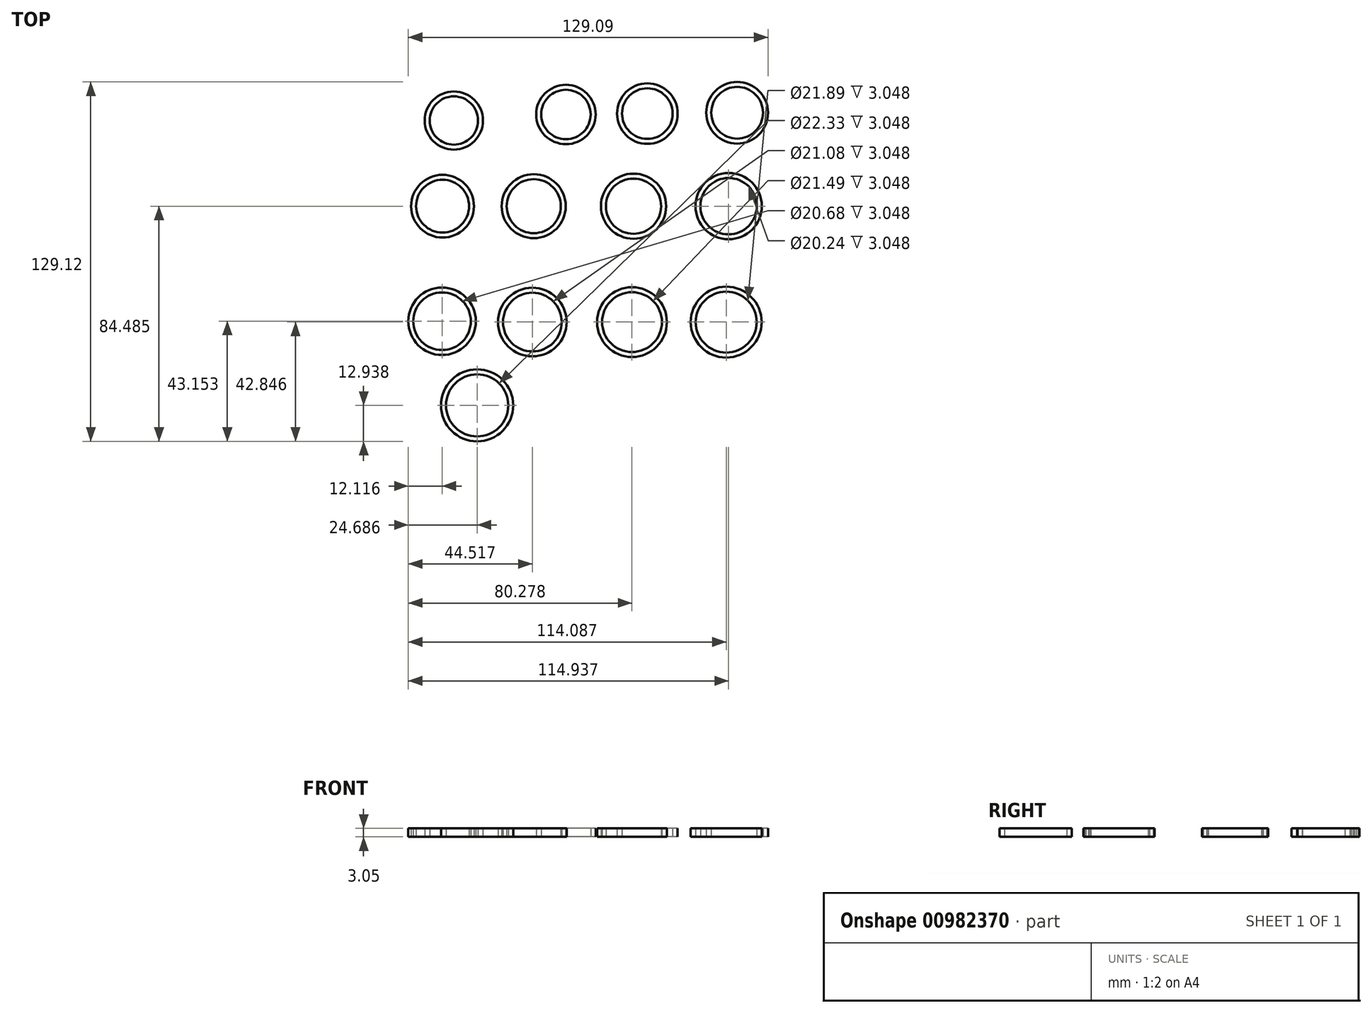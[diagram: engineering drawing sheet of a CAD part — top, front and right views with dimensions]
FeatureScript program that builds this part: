
annotation { "Feature Type Name" : "Feature", "Feature Type Description" : "" }
export const myFeature = defineFeature(function(context is Context, id is Id, definition is map)
    precondition{}
    {
        {
            var Q0;
            Q0=qCreatedBy(makeId("Top.planeOp"),FACE);
            var sketch = newSketch(context, id + "F0", { "sketchPlane" : qUnion([Q0])});
            skCircle(sketch, "E0", {"center": v(-50.04, 48.2) * mm, "radius": 8.67 * mm});
            skCircle(sketch, "E1", {"center": v(-50.04, 48.2) * mm, "radius": 10.45 * mm});
            skSolve(sketch);
        }
        {
            var Q0;
            Q0 = qSketchRegion(id + "F0", true);
            extrude(context, id + "F1", {"entities" : qUnion([Q0]), "depth" : 3.05 * mm, "offsetDistance" : 25.4 * mm});
        }
        {
            var Q0;
            Q0=qCreatedBy(makeId("Top.planeOp"),FACE);
            var sketch = newSketch(context, id + "F2", { "sketchPlane" : qUnion([Q0])});
            skCircle(sketch, "E2", {"center": v(-9.83, 50.36) * mm, "radius": 8.88 * mm});
            skCircle(sketch, "E3", {"center": v(-9.83, 50.36) * mm, "radius": 10.66 * mm});
            skSolve(sketch);
        }
        {
            var Q0;
            Q0 = qSketchRegion(id + "F2", true);
            extrude(context, id + "F3", {"entities" : qUnion([Q0]), "depth" : 3.05 * mm, "offsetDistance" : 25.4 * mm});
        }
        {
            var Q0;
            Q0=qCreatedBy(makeId("Top.planeOp"),FACE);
            var sketch = newSketch(context, id + "F4", { "sketchPlane" : qUnion([Q0])});
            skCircle(sketch, "E4", {"center": v(19.4, 50.69) * mm, "radius": 10.87 * mm});
            skCircle(sketch, "E5", {"center": v(19.4, 50.69) * mm, "radius": 9.1 * mm});
            skSolve(sketch);
        }
        {
            var Q0;
            Q0 = qSketchRegion(id + "F4", true);
            extrude(context, id + "F5", {"entities" : qUnion([Q0]), "depth" : 3.05 * mm, "offsetDistance" : 25.4 * mm});
        }
        {
            var Q0;
            Q0=qCreatedBy(makeId("Top.planeOp"),FACE);
            var sketch = newSketch(context, id + "F6", { "sketchPlane" : qUnion([Q0])});
            skCircle(sketch, "E6", {"center": v(-54.08, 17.43) * mm, "radius": 11.28 * mm});
            skCircle(sketch, "E7", {"center": v(-21.36, 17.43) * mm, "radius": 11.48 * mm});
            skCircle(sketch, "E8", {"center": v(14.44, 17.43) * mm, "radius": 11.7 * mm});
            skCircle(sketch, "E9", {"center": v(48.56, 17.43) * mm, "radius": 11.9 * mm});
            skCircle(sketch, "E10", {"center": v(51.63, 51) * mm, "radius": 11.07 * mm});
            skCircle(sketch, "E11", {"center": v(51.63, 51) * mm, "radius": 9.3 * mm});
            skCircle(sketch, "E12", {"center": v(-54.08, 17.43) * mm, "radius": 9.5 * mm});
            skCircle(sketch, "E13", {"center": v(-21.36, 17.43) * mm, "radius": 9.7 * mm});
            skCircle(sketch, "E14", {"center": v(14.44, 17.43) * mm, "radius": 9.92 * mm});
            skCircle(sketch, "E15", {"center": v(48.56, 17.43) * mm, "radius": 10.12 * mm});
            skSolve(sketch);
        }
        {
            var Q0;
            Q0=makeQuery(id+"F6.imprint","IMPRINT",FACE,{"disambiguationData":[TD([[makeQuery(id+"F6.imprint","IMPRINT",EDGE,{"derivedFrom":sQuery(id+"F6.wireOp",EDGE,"E10")}),1.0]])]});
            extrude(context, id + "F7", {"entities" : qUnion([Q0]), "depth" : 3.05 * mm, "offsetDistance" : 25.4 * mm});
        }
        {
            var Q0;
            Q0=makeQuery(id+"F6.imprint","IMPRINT",FACE,{"disambiguationData":[TD([[makeQuery(id+"F6.imprint","IMPRINT",EDGE,{"derivedFrom":sQuery(id+"F6.wireOp",EDGE,"E6")}),1.0]])]});
            extrude(context, id + "F8", {"entities" : qUnion([Q0]), "depth" : 3.05 * mm, "offsetDistance" : 25.4 * mm});
        }
        {
            var Q0;
            Q0=makeQuery(id+"F6.imprint","IMPRINT",FACE,{"disambiguationData":[TD([[makeQuery(id+"F6.imprint","IMPRINT",EDGE,{"derivedFrom":sQuery(id+"F6.wireOp",EDGE,"E7")}),1.0]])]});
            extrude(context, id + "F9", {"entities" : qUnion([Q0]), "depth" : 3.05 * mm, "offsetDistance" : 25.4 * mm});
        }
        {
            var Q0;
            Q0=makeQuery(id+"F6.imprint","IMPRINT",FACE,{"disambiguationData":[TD([[makeQuery(id+"F6.imprint","IMPRINT",EDGE,{"derivedFrom":sQuery(id+"F6.wireOp",EDGE,"E8")}),1.0]])]});
            extrude(context, id + "F10", {"entities" : qUnion([Q0]), "depth" : 3.05 * mm, "offsetDistance" : 25.4 * mm});
        }
        {
            var Q0;
            Q0=makeQuery(id+"F6.imprint","IMPRINT",FACE,{"disambiguationData":[TD([[makeQuery(id+"F6.imprint","IMPRINT",EDGE,{"derivedFrom":sQuery(id+"F6.wireOp",EDGE,"E9")}),1.0]])]});
            extrude(context, id + "F11", {"entities" : qUnion([Q0]), "depth" : 3.05 * mm, "offsetDistance" : 25.4 * mm});
        }
        {
            var Q0;
            Q0=qCreatedBy(makeId("Top.planeOp"),FACE);
            var sketch = newSketch(context, id + "F12", { "sketchPlane" : qUnion([Q0])});
            skCircle(sketch, "E16", {"center": v(-54.26, -23.9) * mm, "radius": 12.12 * mm});
            skCircle(sketch, "E17", {"center": v(-54.26, -23.9) * mm, "radius": 10.34 * mm});
            skCircle(sketch, "E18", {"center": v(-21.86, -24.2) * mm, "radius": 12.32 * mm});
            skCircle(sketch, "E19", {"center": v(-21.86, -24.2) * mm, "radius": 10.54 * mm});
            skCircle(sketch, "E20", {"center": v(13.9, -24.2) * mm, "radius": 12.52 * mm});
            skCircle(sketch, "E21", {"center": v(13.9, -24.2) * mm, "radius": 10.74 * mm});
            skCircle(sketch, "E22", {"center": v(47.7, -24.2) * mm, "radius": 10.95 * mm});
            skCircle(sketch, "E23", {"center": v(47.7, -24.2) * mm, "radius": 12.73 * mm});
            skCircle(sketch, "E24", {"center": v(-41.7, -54.11) * mm, "radius": 12.94 * mm});
            skCircle(sketch, "E25", {"center": v(-41.7, -54.11) * mm, "radius": 11.16 * mm});
            skSolve(sketch);
        }
        {
            var Q0;
            Q0=makeQuery(id+"F12.imprint","IMPRINT",FACE,{"disambiguationData":[TD([[makeQuery(id+"F12.imprint","IMPRINT",EDGE,{"derivedFrom":sQuery(id+"F12.wireOp",EDGE,"E16")}),1.0]])]});
            extrude(context, id + "F13", {"entities" : qUnion([Q0]), "depth" : 3.05 * mm, "offsetDistance" : 25.4 * mm});
        }
        {
            var Q0;
            Q0=makeQuery(id+"F12.imprint","IMPRINT",FACE,{"disambiguationData":[TD([[makeQuery(id+"F12.imprint","IMPRINT",EDGE,{"derivedFrom":sQuery(id+"F12.wireOp",EDGE,"E18")}),1.0]])]});
            extrude(context, id + "F14", {"entities" : qUnion([Q0]), "depth" : 3.05 * mm, "offsetDistance" : 25.4 * mm});
        }
        {
            var Q0;
            Q0=makeQuery(id+"F12.imprint","IMPRINT",FACE,{"disambiguationData":[TD([[makeQuery(id+"F12.imprint","IMPRINT",EDGE,{"derivedFrom":sQuery(id+"F12.wireOp",EDGE,"E20")}),1.0]])]});
            extrude(context, id + "F15", {"entities" : qUnion([Q0]), "depth" : 3.05 * mm, "offsetDistance" : 25.4 * mm});
        }
        {
            var Q0;
            Q0=makeQuery(id+"F12.imprint","IMPRINT",FACE,{"disambiguationData":[TD([[makeQuery(id+"F12.imprint","IMPRINT",EDGE,{"derivedFrom":sQuery(id+"F12.wireOp",EDGE,"E22")}),-1.0]])]});
            extrude(context, id + "F16", {"entities" : qUnion([Q0]), "depth" : 3.05 * mm, "offsetDistance" : 25.4 * mm});
        }
        {
            var Q0;
            Q0=makeQuery(id+"F12.imprint","IMPRINT",FACE,{"disambiguationData":[TD([[makeQuery(id+"F12.imprint","IMPRINT",EDGE,{"derivedFrom":sQuery(id+"F12.wireOp",EDGE,"E24")}),1.0]])]});
            extrude(context, id + "F17", {"entities" : qUnion([Q0]), "depth" : 3.05 * mm, "offsetDistance" : 25.4 * mm});
        }
    });
